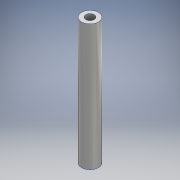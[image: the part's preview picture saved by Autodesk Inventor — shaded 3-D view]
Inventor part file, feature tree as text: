
AUTODESK INVENTOR PART (.ipt)
format: ipt  version: 2016 (Build 200138000, 138)  size: 92,672 bytes
history: native  units: mm
features: other x1, extrude x1, sketch x1
ambient origin geometry x8: Origin, YZ Plane, XZ Plane, XY Plane, X Axis, Y Axis, Z Axis, Center Point
bodies: Body1 (feature_tree)
feature tree (3):
  other  "ソリッド1"
  extrude  "押し出し1"  Depth=4.0mm
  sketch  "スケッチ1"
